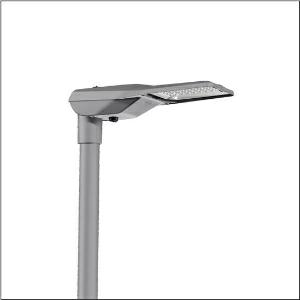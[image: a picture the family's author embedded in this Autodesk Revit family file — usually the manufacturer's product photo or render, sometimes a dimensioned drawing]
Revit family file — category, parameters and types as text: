
# Revit family: streetlight_sl_21_iq_mini___st1_5a_5xe2p31y08hb_ad09
name_source: partatom
category: Lighting Fixtures
units: mm (PartAtom-declared; Revit-internal decimal feet)

## family parameters
Cut with Voids When Loaded = No
Host = Face
Light Source = No
Part Type = Normal
Room Calculation Point = No
Round Connector Dimension = Use Diameter
Shared = No

## types (1)
- --- (1 x LED, 9580 lm, 71 W, 3000K)
    Apparent Load = 71 VA
    CIE Flux Codes = 22 53 95 100 100
    Color Rendering = 70
    Color Temperature = 3000K
    Default Elevation = 1800 mm
    Description = Streetlight SL 21 iQ mini, mast luminaire, primary light control with lens, of PMMA, primary optical cover: cover, of toughened safety glass, transparent, light distribution: ST1.5a, light emission: direct distribution, primary light characteristic: asymmetric, installation type: post-top, side-entry, LED, High Power LED, rated luminous flux: 9.580lm, luminous efficacy: 135lm/W, light colour: 730, colour temperature: 3000K, control: presetting dimming logarithmic, Street-Remote, Auto-Match, Temp-Guard, Lumen-Switch, Night-Set, Smart-Wire, Light-Fading, Desk-Remote (wireless, voltage-free reading and setting of iQ features in the workshop via application-optimized NFC function/RFID function), optimised constant luminous flux control (CLO 2.0), mains connection: 220..240V, AC, 50/60Hz, start of lifetime: 71W, end of service life: 75W, reduction: 30W, luminaire housing, of diecast aluminium, powder-coated, Siteco® metallic grey (DB 702S), corrosivity category C5 mid according to DIN EN ISO 12944, please order mast flange separately, inclination adjustable: 0°, 5°, 10°, 15°, sealing non-destructively replaceable, multi-level sealing system, length: 628mm, width: 235mm, height: 110mm, mast flange for spigot size: 42mm (side-entry): 5XC10008XM4, 60/48mm (side-entry/post-top): 5XC10108XM2, 76/60mm (side-entry/post-top): 5XC10108XM1, Smart Interface below and above, protection rating (complete): IP66, insulation class (complete): insulation class II (safety insulation), certification: CE, ENEC, ENEC+, VDE, impact resistance: IK09, permissible operating ambient temperature for outdoor applications: -40..+50°C, standard-compliant lighting for roads and squares, packaging unit: 1 piece

Light Distribution: ST1.5a
    Height = 110 mm
    Lamp = 1 x LED
    Lamp Light Flux = 9580 lm
    Lamp Power = 71 W
    Lamp count = 1
    Length = 625 mm
    Luminous efficacy = 135 lm/W
    Manufacturer = Siteco
    ModVariant = No
    Model = 5XE2P31Y08HB
    Number of Poles = 1
    OnlyDefault = Yes
    Power Factor = 1
    Product Name = Streetlight SL 21 iQ mini | ST1.5a
    Product group = mast luminaire | pylon top
    ProductGroupID = 6100
    Protection Class = Protection class II
    Protection Degree = IP 66
    RLX_Detail_Level = 1
    RLX_Emergency_Light_Flux = 0 lm
    RLX_Emergency_Type = 0
    RLX_Emergency_Type_DB = No
    RlxData = <blob elided: 96041 chars, md5=cd554366>
    Socket = socket
    Standby Power = 0 W
    System Light Flux = 9580 lm
    System Power = 71 W
    Type Comments = factory setting: luminous flux: 100 % | dim-lin: 254 | 716 mA
    Type Image = l_1003514.jpg
    URL = http://relux.com
    VarID = @adj_041987
    Voltage = 0 V
    Weight = 0.00 kg
    Width = 234 mm

## geometry (parser evidence)
native form markers: Blend x4, Sweep x9
no freeform markers — native parametric forms only
